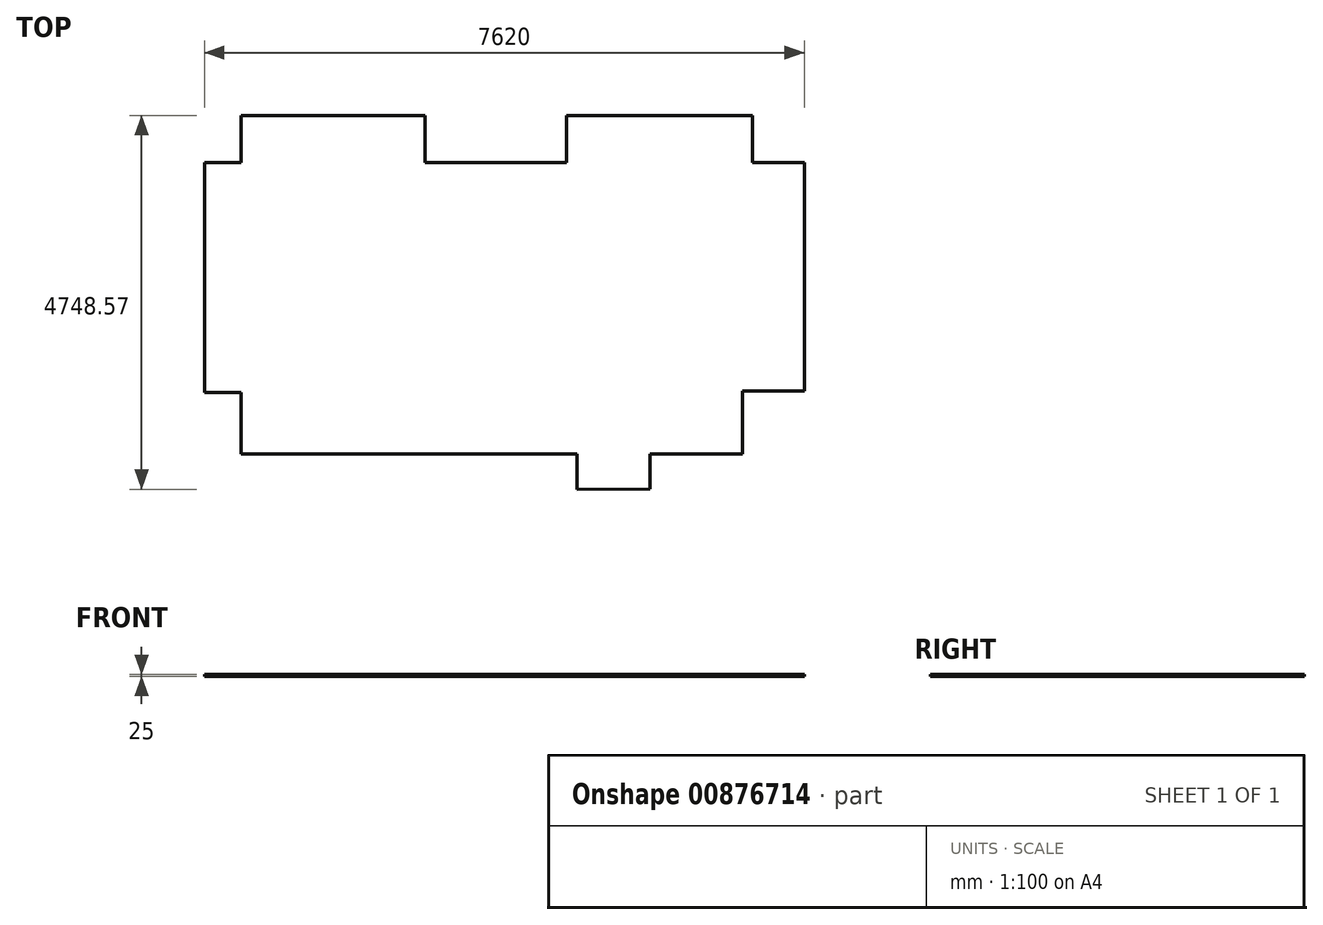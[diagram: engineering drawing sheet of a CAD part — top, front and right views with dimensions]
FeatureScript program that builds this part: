
annotation { "Feature Type Name" : "Feature", "Feature Type Description" : "" }
export const myFeature = defineFeature(function(context is Context, id is Id, definition is map)
    precondition{}
    {
        {
            var Q0;
            Q0=qCreatedBy(makeId("Top.planeOp"),FACE);
            var sketch = newSketch(context, id + "F0", { "sketchPlane" : qUnion([Q0])});
            skLineSegment(sketch, "E0", {"start": v(0, 0) * mm, "end": v(-2335, 0) * mm});
            skLineSegment(sketch, "E1", {"start": v(-2335, 0) * mm, "end": v(-2335, -600) * mm});
            skLineSegment(sketch, "E2", {"start": v(0, 0) * mm, "end": v(0, -600) * mm});
            skLineSegment(sketch, "E3", {"start": v(-2335, -600) * mm, "end": v(-2801.37, -600) * mm});
            skLineSegment(sketch, "E4", {"start": v(-2801.37, -600) * mm, "end": v(-2801.37, -3520) * mm});
            skLineSegment(sketch, "E5", {"start": v(-2801.37, -3520) * mm, "end": v(-2335, -3520) * mm});
            skLineSegment(sketch, "E6", {"start": v(-2335, -3520) * mm, "end": v(-2335, -4300) * mm});
            skLineSegment(sketch, "E7", {"start": v(-2335, -4300) * mm, "end": v(1932, -4300) * mm});
            skLineSegment(sketch, "E8", {"start": v(0, -600) * mm, "end": v(1800, -600) * mm});
            skLineSegment(sketch, "E9", {"start": v(1800, -600) * mm, "end": v(1800, 0) * mm});
            skLineSegment(sketch, "E10", {"start": v(1800, 0) * mm, "end": v(4160, 0) * mm});
            skLineSegment(sketch, "E11", {"start": v(4160, 0) * mm, "end": v(4160, -600) * mm});
            skLineSegment(sketch, "E12", {"start": v(4160, -600) * mm, "end": v(4818.63, -600) * mm});
            skLineSegment(sketch, "E13", {"start": v(4818.63, -600) * mm, "end": v(4818.63, -3500) * mm});
            skLineSegment(sketch, "E14", {"start": v(4818.63, -3500) * mm, "end": v(4031.1, -3500) * mm});
            skLineSegment(sketch, "E15", {"start": v(4031.1, -3500) * mm, "end": v(4031.1, -4300) * mm});
            skLineSegment(sketch, "E16", {"start": v(4031.1, -4300) * mm, "end": v(3629.9, -4300) * mm});
            skLineSegment(sketch, "E17", {"start": v(3629.9, -4300) * mm, "end": v(2858.47, -4300) * mm});
            skLineSegment(sketch, "E18", {"start": v(1932, -4300) * mm, "end": v(1932, -4748.57) * mm});
            skLineSegment(sketch, "E19", {"start": v(2858.47, -4300) * mm, "end": v(2858.47, -4746.12) * mm});
            skLineSegment(sketch, "E20", {"start": v(2858.47, -4746.12) * mm, "end": v(1932, -4748.57) * mm});
            skSolve(sketch);
        }
        {
            var Q0;
            Q0=makeQuery(id+"F0.imprint","IMPRINT",FACE,{"disambiguationData":[TD([[makeQuery(id+"F0.imprint","IMPRINT",EDGE,{"derivedFrom":sQuery(id+"F0.wireOp",EDGE,"E0")}),1.0]])]});
            extrude(context, id + "F1", {"entities" : qUnion([Q0]), "depth" : 25 * mm, "offsetDistance" : 25 * mm});
        }
    });
